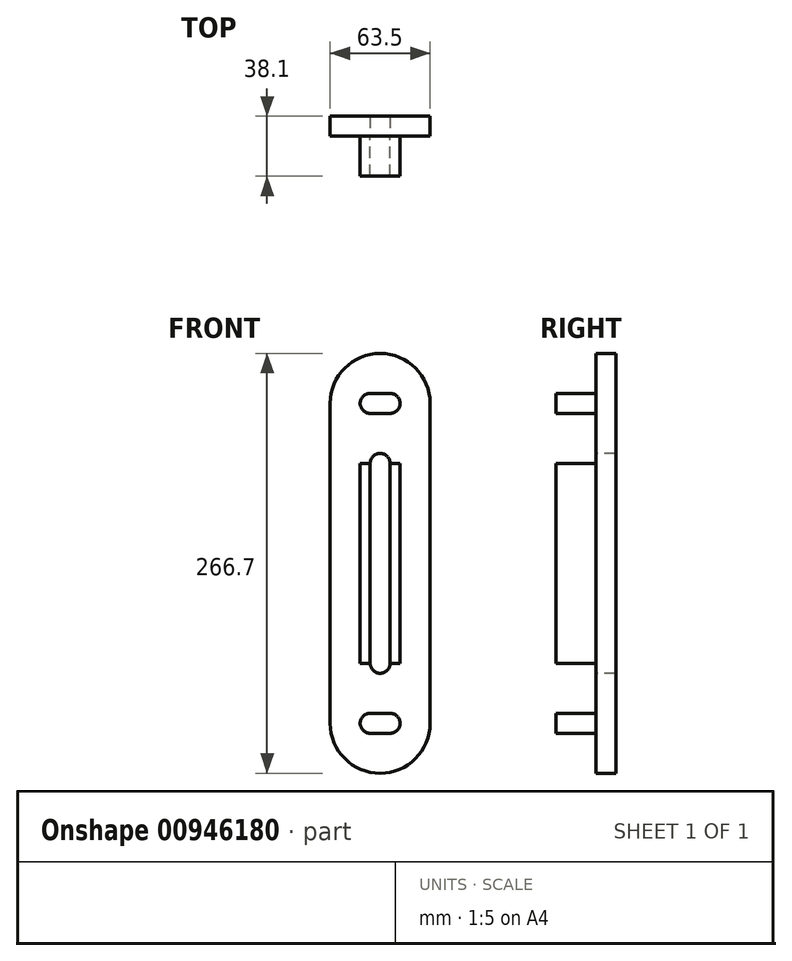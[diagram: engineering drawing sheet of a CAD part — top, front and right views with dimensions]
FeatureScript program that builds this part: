
annotation { "Feature Type Name" : "Feature", "Feature Type Description" : "" }
export const myFeature = defineFeature(function(context is Context, id is Id, definition is map)
    precondition{}
    {
        {
            var Q0;
            Q0=qCreatedBy(makeId("Front.planeOp"),FACE);
            var sketch = newSketch(context, id + "F0", { "sketchPlane" : qUnion([Q0])});
            skLineSegment(sketch, "E0.bottom", {"start": v(-1.99, 30.73) * mm, "end": v(10.71, 30.73) * mm});
            skLineSegment(sketch, "E0.top", {"start": v(-1.99, 18.03) * mm, "end": v(10.71, 18.03) * mm});
            skPoint(sketch, "E0.middle", {"position": v(4.36, 24.38) * mm});
            skArc(sketch, "E1", {"start": v(10.71, 30.73) * mm, "mid": v(17.06, 24.38) * mm, "end": v(10.71, 18.03) * mm});
            skArc(sketch, "E2", {"start": v(-1.99, 30.73) * mm, "mid": v(-8.34, 24.38) * mm, "end": v(-1.99, 18.03) * mm});
            skLineSegment(sketch, "E3.bottom", {"start": v(-1.99, -172.47) * mm, "end": v(10.71, -172.47) * mm});
            skLineSegment(sketch, "E3.top", {"start": v(-1.99, -185.17) * mm, "end": v(10.71, -185.17) * mm});
            skPoint(sketch, "E3.middle", {"position": v(4.36, -178.82) * mm});
            skArc(sketch, "E4", {"start": v(10.71, -172.47) * mm, "mid": v(17.06, -178.82) * mm, "end": v(10.71, -185.17) * mm});
            skArc(sketch, "E5", {"start": v(-1.99, -172.47) * mm, "mid": v(-8.34, -178.82) * mm, "end": v(-1.99, -185.17) * mm});
            skSolve(sketch);
        }
        {
            var Q0;
            Q0=qSketchRegion(id+"F0",true);
            extrude(context, id + "F1", {"entities" : qUnion([Q0]), "depth" : 25.4 * mm, "offsetDistance" : 25.4 * mm});
        }
        {
            var Q0;
            Q0=makeQuery(id+"F1.opExtrude","CAP_FACE",FACE,{"disambiguationData":[OSD([sQuery(id+"F0.wireOp",EDGE,"E0.bottom"),sQuery(id+"F0.wireOp",EDGE,"E0.top"),sQuery(id+"F0.wireOp",EDGE,"E1"),sQuery(id+"F0.wireOp",EDGE,"E2")])],"isStart":true});
            var sketch = newSketch(context, id + "F2", { "sketchPlane" : qUnion([Q0])});
            skPoint(sketch, "E6.firstSnap0", {"position": v(-17.06, 24.38) * mm});
            skLineSegment(sketch, "E6.left", {"start": v(-36.11, 24.38) * mm, "end": v(-36.11, -178.82) * mm});
            skLineSegment(sketch, "E6.right", {"start": v(27.39, 24.38) * mm, "end": v(27.39, -178.82) * mm});
            skArc(sketch, "E7", {"start": v(27.39, 24.38) * mm, "mid": v(-4.36, 56.13) * mm, "end": v(-36.11, 24.38) * mm});
            skArc(sketch, "E8", {"start": v(27.39, -178.82) * mm, "mid": v(-4.36, -210.57) * mm, "end": v(-36.11, -178.82) * mm});
            skLineSegment(sketch, "E9.left", {"start": v(-10.71, -13.72) * mm, "end": v(-10.71, -140.72) * mm});
            skLineSegment(sketch, "E9.right", {"start": v(1.99, -13.72) * mm, "end": v(1.99, -140.72) * mm});
            skArc(sketch, "E10", {"start": v(-10.71, -13.72) * mm, "mid": v(-4.36, -7.37) * mm, "end": v(1.99, -13.72) * mm});
            skArc(sketch, "E11", {"start": v(-10.71, -140.72) * mm, "mid": v(-4.36, -147.07) * mm, "end": v(1.99, -140.72) * mm});
            skSolve(sketch);
        }
        {
            var Q0;
            Q0 = qSketchRegion(id + "F2", true);
            extrude(context, id + "F3", {"entities" : qUnion([Q0]), "depth" : 12.7 * mm, "offsetDistance" : 25.4 * mm});
        }
        {
            var Q0;
            Q0=makeQuery(id+"F3.opExtrude","CAP_FACE",FACE,{"disambiguationData":[OSD([sQuery(id+"F2.wireOp",EDGE,"E6.left"),sQuery(id+"F2.wireOp",EDGE,"E6.right"),sQuery(id+"F2.wireOp",EDGE,"E7"),sQuery(id+"F2.wireOp",EDGE,"E8"),sQuery(id+"F2.wireOp",EDGE,"E9.left"),sQuery(id+"F2.wireOp",EDGE,"E9.right"),sQuery(id+"F2.wireOp",EDGE,"E10"),sQuery(id+"F2.wireOp",EDGE,"E11")])],"isStart":true});
            var sketch = newSketch(context, id + "F4", { "sketchPlane" : qUnion([Q0])});
            skLineSegment(sketch, "E12.bottom", {"start": v(10.71, -13.72) * mm, "end": v(17.06, -13.72) * mm});
            skLineSegment(sketch, "E12.top", {"start": v(10.71, -140.72) * mm, "end": v(17.06, -140.72) * mm});
            skLineSegment(sketch, "E12.left", {"start": v(10.71, -13.72) * mm, "end": v(10.71, -140.72) * mm});
            skLineSegment(sketch, "E12.right", {"start": v(17.06, -13.72) * mm, "end": v(17.06, -140.72) * mm});
            skLineSegment(sketch, "E13.bottom", {"start": v(-1.99, -13.72) * mm, "end": v(-8.34, -13.72) * mm});
            skLineSegment(sketch, "E13.top", {"start": v(-1.99, -140.72) * mm, "end": v(-8.34, -140.72) * mm});
            skLineSegment(sketch, "E13.left", {"start": v(-1.99, -13.72) * mm, "end": v(-1.99, -140.72) * mm});
            skLineSegment(sketch, "E13.right", {"start": v(-8.34, -13.72) * mm, "end": v(-8.34, -140.72) * mm});
            skSolve(sketch);
        }
        {
            var Q0;
            Q0 = qSketchRegion(id + "F4", true);
            extrude(context, id + "F5", {"entities" : qUnion([Q0]), "operationType" : NewBodyOperationType.ADD, "depth" : 25.4 * mm, "offsetDistance" : 25.4 * mm});
        }
    });
